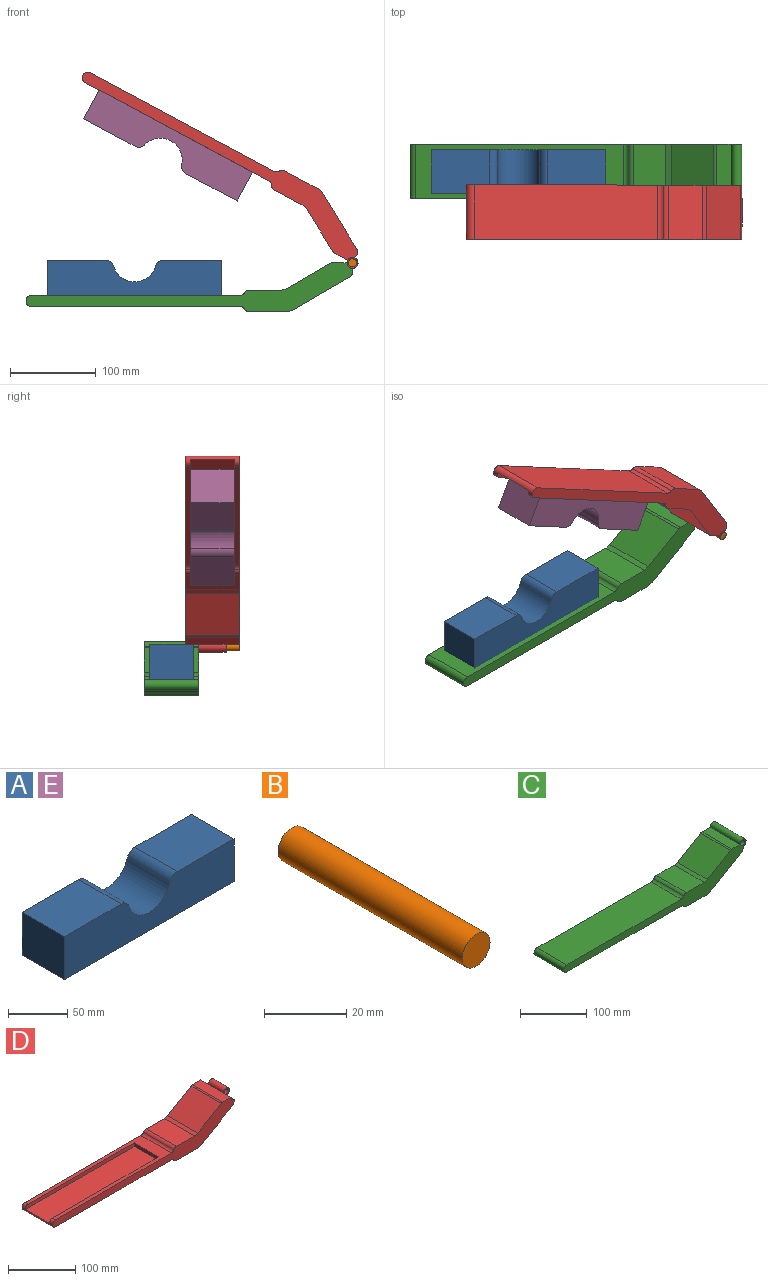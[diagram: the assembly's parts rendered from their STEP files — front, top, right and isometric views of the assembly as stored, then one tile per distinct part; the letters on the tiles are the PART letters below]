
ASSEMBLY  parts=5 mates=3
PART A: 10 faces, bbox 203.2x50.8x44.5 mm
  f0: cylinder r=25.4mm len=50.8mm, axis (0,1,0), area 3340.8mm2, adj f1,f7,f8,f9
  f1: cylinder r=9.53mm len=50.8mm, axis (0,1,0), area 626.4mm2, adj f0,f2,f8,f9
  f2: plane 68x50.8mm, normal (0,0,1), area 3454.3mm2, adj f1,f3,f8,f9
  f3: plane 50.8x44.45mm, normal (-1,0,0), area 2258.1mm2, adj f2,f4,f8,f9
  f4: plane 203.2x50.8mm, normal (0,0,-1), area 10322.6mm2, adj f3,f5,f8,f9
  f5: plane 50.8x44.45mm, normal (1,0,0), area 2258.1mm2, adj f4,f6,f8,f9
  f6: plane 68x50.8mm, normal (0,0,1), area 3454.3mm2, adj f5,f7,f8,f9
  f7: cylinder r=9.53mm len=50.8mm, axis (0,1,0), area 626.4mm2, adj f0,f6,f8,f9
  f8: plane 203.2x44.45mm, normal (0,-1,0), area 7994.4mm2, adj f0,f1,f2,f3,f4,f5,f6,f7
  f9: plane 203.2x44.45mm, normal (0,1,0), area 7994.4mm2, adj f0,f1,f2,f3,f4,f5,f6,f7
PART B: 3 faces, bbox 9.5x63.5x9.5 mm
  f0: cylinder r=4.76mm len=63.5mm, axis (0,1,0), area 1900.2mm2, adj f1,f2
  f1: plane 9.53x9.53mm, normal (0,-1,0), area 71.3mm2, adj f0
  f2: plane 9.53x9.53mm, normal (0,1,0), area 71.3mm2, adj f0
PART C: 21 faces, bbox 387.4x63.5x63.5 mm
  f0: plane 243x63.5mm, normal (0,0,1), area 15430.6mm2, adj f1,f18,f19,f20
  f1: cylinder r=6.35mm len=63.5mm, axis (0,1,0), area 1266.8mm2, adj f0,f2,f19,f20
  f2: plane 243x63.5mm, normal (0,0,-1), area 15430.6mm2, adj f1,f3,f19,f20
  f3: cylinder r=6.35mm len=63.5mm, axis (0,1,0), area 422.3mm2, adj f2,f4,f19,f20
  f4: cylinder r=6.35mm len=63.5mm, axis (0,1,0), area 422.3mm2, adj f3,f5,f19,f20
  f5: plane 63.5x44.45mm, normal (0,0,-1), area 2822.6mm2, adj f4,f6,f19,f20
  f6: plane 63.5x6.4mm, normal (0.26,0,-0.97), area 420.9mm2, adj f5,f7,f19,f20
  f7: plane 66.65x63.5mm, normal (0.5,0,-0.86), area 4899.8mm2, adj f6,f8,f19,f20
  f8: cylinder r=6.35mm len=63.5mm, axis (0,1,0), area 420.5mm2, adj f7,f9,f19,f20
  f9: plane 63.5x4.71mm, normal (1,0,0), area 298.8mm2, adj f8,f10,f19,f20
  f10: cylinder r=6.35mm len=63.5mm, axis (0,1,0), area 1900.2mm2, adj f9,f11,f19,f20
  f11: plane 63.5x17.14mm, normal (0,0,1), area 1088.3mm2, adj f10,f12,f19,f20
  f12: cylinder r=6.35mm len=63.5mm, axis (0,1,0), area 212.9mm2, adj f11,f13,f19,f20
  f13: plane 63.5x49.51mm, normal (-0.5,0,0.86), area 3639.9mm2, adj f12,f14,f19,f20
  f14: plane 63.5x6.4mm, normal (-0.3,0,0.95), area 425.8mm2, adj f13,f15,f19,f20
  f15: plane 63.5x38.05mm, normal (0,0,1), area 2416.2mm2, adj f14,f16,f19,f20
  f16: cylinder r=6.35mm len=63.5mm, axis (0,1,0), area 422.3mm2, adj f15,f18,f19,f20
  f17: cylinder r=4.76mm len=63.5mm, axis (0,1,0), area 1900.2mm2, adj f19,f20
  f18: cylinder r=6.35mm len=63.5mm, axis (0,1,0), area 422.3mm2, adj f0,f16,f19,f20
  f19: plane 387.35x63.5mm, normal (0,-1,0), area 6564.8mm2, adj f0,f1,f2,f3,f4,f5,f6,f7
  f20: plane 387.35x63.5mm, normal (0,1,0), area 6564.8mm2, adj f0,f1,f2,f3,f4,f5,f6,f7
PART D: 29 faces, bbox 387.4x63.5x63.5 mm
  f0: plane 243x63.5mm, normal (0,0,1), area 4140.3mm2, adj f1,f18,f19,f20,f26,f27,f28
  f1: cylinder r=6.35mm len=63.5mm, axis (0,1,0), area 760.1mm2, adj f0,f4,f19,f20,f25,f26,f28
  f2: cylinder r=4.76mm len=31.75mm, axis (0,1,0), area 950.1mm2, adj f22,f24
  f3: cylinder r=6.35mm len=31.75mm, axis (0,1,0), area 950.1mm2, adj f11,f12,f22,f24
  f4: plane 243x63.5mm, normal (0,0,-1), area 15430.6mm2, adj f1,f5,f19,f20
  f5: cylinder r=6.35mm len=63.5mm, axis (0,1,0), area 422.3mm2, adj f4,f6,f19,f20
  f6: cylinder r=6.35mm len=63.5mm, axis (0,1,0), area 422.3mm2, adj f5,f7,f19,f20
  f7: plane 63.5x44.45mm, normal (0,0,-1), area 2822.6mm2, adj f6,f8,f19,f20
  f8: plane 63.5x6.4mm, normal (0.26,0,-0.97), area 420.9mm2, adj f7,f9,f19,f20
  f9: plane 66.65x63.5mm, normal (0.5,0,-0.86), area 4899.8mm2, adj f8,f10,f19,f20
  f10: cylinder r=6.35mm len=63.5mm, axis (0,1,0), area 420.5mm2, adj f9,f11,f19,f20
  f11: plane 63.5x4.71mm, normal (1,0,0), area 298.8mm2, adj f3,f10,f19,f20,f21,f23
  f12: plane 63.5x17.14mm, normal (0,0,1), area 1088.3mm2, adj f3,f13,f19,f20,f21,f23
  f13: cylinder r=6.35mm len=63.5mm, axis (0,1,0), area 212.9mm2, adj f12,f14,f19,f20
  f14: plane 63.5x49.51mm, normal (-0.5,0,0.86), area 3639.9mm2, adj f13,f15,f19,f20
  f15: plane 63.5x6.4mm, normal (-0.3,0,0.95), area 425.8mm2, adj f14,f16,f19,f20
  f16: plane 63.5x38.05mm, normal (0,0,1), area 2416.2mm2, adj f15,f17,f19,f20
  f17: cylinder r=6.35mm len=63.5mm, axis (0,1,0), area 422.3mm2, adj f16,f18,f19,f20
  f18: cylinder r=6.35mm len=63.5mm, axis (0,1,0), area 422.3mm2, adj f0,f17,f19,f20
  f19: plane 381x57.15mm, normal (0,-1,0), area 6509.4mm2, adj f0,f1,f4,f5,f6,f7,f8,f9
  f20: plane 381x57.15mm, normal (0,1,0), area 6509.4mm2, adj f0,f1,f4,f5,f6,f7,f8,f9
  f21: cylinder r=6.35mm len=15.88mm, axis (0,-1,0), area 158.3mm2, adj f11,f12,f19,f22
  f22: plane 12.7x12.7mm, normal (0,-1,0), area 55.4mm2, adj f2,f3,f21
  f23: cylinder r=6.35mm len=15.88mm, axis (0,1,0), area 158.3mm2, adj f11,f12,f20,f24
  f24: plane 12.7x12.7mm, normal (0,1,0), area 55.4mm2, adj f2,f3,f23
  f25: plane 228.6x50.8mm, normal (0,0,1), area 11612.9mm2, adj f1,f26,f27,f28
  f26: plane 228.6x6.35mm, normal (0,1,0), area 1443mm2, adj f0,f1,f25,f27
  f27: plane 50.8x6.35mm, normal (-1,0,0), area 322.6mm2, adj f0,f25,f26,f28
  f28: plane 228.6x6.35mm, normal (0,-1,0), area 1443mm2, adj f0,f1,f25,f27
PART E: same geometry as A
PLACE A t=(-279.59,-51.11,75.68)mm
PLACE B t=(-25.25,-92.39,97.01)mm
PLACE C t=(-25.25,-76.51,94.73)mm fixed
PLACE D rot(axis=(0.97,0,-0.24),180deg) t=(-25.25,-124.14,94.73)mm
PLACE E rot(axis=(0,-1,0),151.8deg) t=(-238.94,-98.74,234.46)mm
MATE revolute D.f2 <-> C.f10  axis (0,-1,0) through (-25.25,-108.26,94.73)mm
MATE revolute B.f0 <-> D.f2  axis (0,-1,0) through (-25.25,-155.89,94.73)mm
MATE slider E.f3 <-> D.f27  axis (0.88,0,-0.47) through (-138.89,-124.14,206.06)mm
